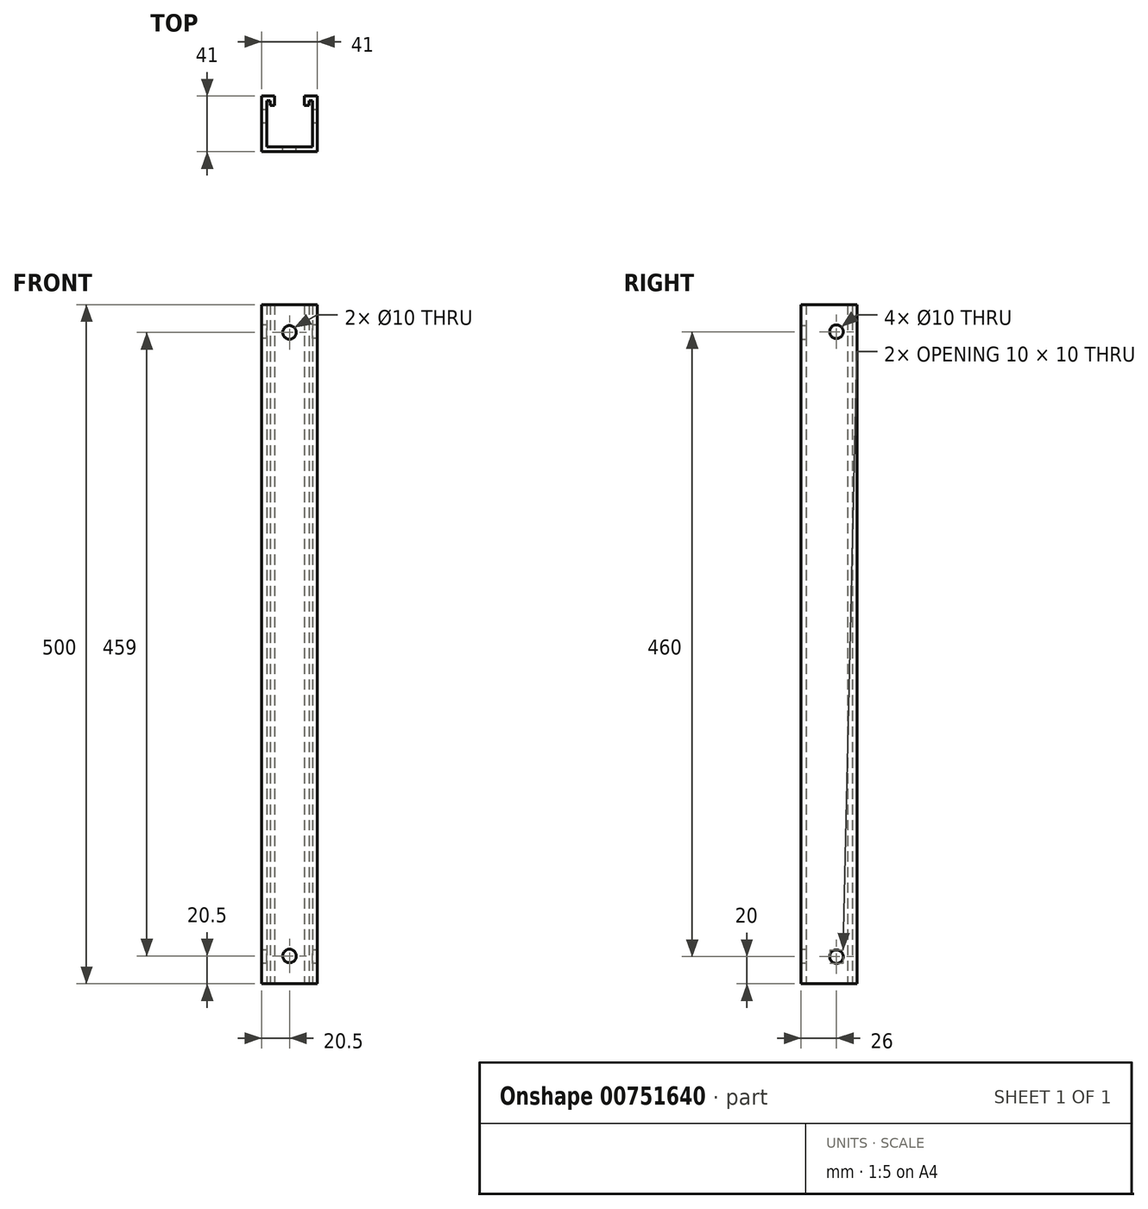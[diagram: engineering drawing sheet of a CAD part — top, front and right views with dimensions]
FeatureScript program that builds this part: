
annotation { "Feature Type Name" : "Feature", "Feature Type Description" : "" }
export const myFeature = defineFeature(function(context is Context, id is Id, definition is map)
    precondition{}
    {
        {
            var Q0;
            Q0=qCreatedBy(makeId("Top.planeOp"),FACE);
            var sketch = newSketch(context, id + "F0", { "sketchPlane" : qUnion([Q0])});
            skLineSegment(sketch, "E0", {"start": v(0, 0) * mm, "end": v(41, 0) * mm});
            skLineSegment(sketch, "E1", {"start": v(41, 0) * mm, "end": v(41, 41) * mm});
            skLineSegment(sketch, "E2", {"start": v(41, 41) * mm, "end": v(31.4, 41) * mm});
            skLineSegment(sketch, "E3", {"start": v(31.4, 41) * mm, "end": v(31.4, 34) * mm});
            skLineSegment(sketch, "E4", {"start": v(31.4, 34) * mm, "end": v(34.8, 34) * mm});
            skLineSegment(sketch, "E5", {"start": v(34.8, 34) * mm, "end": v(34.8, 37.5) * mm});
            skLineSegment(sketch, "E6", {"start": v(34.8, 37.5) * mm, "end": v(37.3, 37.5) * mm});
            skLineSegment(sketch, "E7", {"start": v(37.3, 37.5) * mm, "end": v(37.3, 3.7) * mm});
            skLineSegment(sketch, "E8", {"start": v(37.3, 3.7) * mm, "end": v(3.7, 3.7) * mm});
            skLineSegment(sketch, "E9", {"start": v(0, 0) * mm, "end": v(0, 41) * mm});
            skLineSegment(sketch, "E10", {"start": v(0, 41) * mm, "end": v(9.6, 41) * mm});
            skLineSegment(sketch, "E11", {"start": v(9.6, 41) * mm, "end": v(9.6, 34) * mm});
            skLineSegment(sketch, "E12", {"start": v(9.6, 34) * mm, "end": v(6.2, 34) * mm});
            skLineSegment(sketch, "E13", {"start": v(6.2, 34) * mm, "end": v(6.2, 37.5) * mm});
            skLineSegment(sketch, "E14", {"start": v(6.2, 37.5) * mm, "end": v(3.7, 37.5) * mm});
            skLineSegment(sketch, "E15", {"start": v(3.7, 37.5) * mm, "end": v(3.7, 3.7) * mm});
            skSolve(sketch);
        }
        {
            var Q0;
            Q0=qSketchRegion(id+"F0",true);
            extrude(context, id + "F1", {"entities" : qUnion([Q0]), "depth" : 500 * mm});
        }
        {
            var Q0;
            Q0=makeQuery(id+"F1.opExtrude","SWEPT_FACE",FACE,{"disambiguationData":[OSD([sQuery(id+"F0.wireOp",EDGE,"E8")])]});
            var sketch = newSketch(context, id + "F2", { "sketchPlane" : qUnion([Q0])});
            skCircle(sketch, "E16", {"center": v(-20.5, 479.5) * mm, "radius": 5 * mm});
            skPoint(sketch, "E16.centerSnap0", {"position": v(-20.5, 500) * mm});
            skCircle(sketch, "E17", {"center": v(-20.5, 20.5) * mm, "radius": 5 * mm});
            skPoint(sketch, "E17.centerSnap0", {"position": v(-20.5, 0) * mm});
            skSolve(sketch);
        }
        {
            var Q0;
            Q0=qSketchRegion(id+"F2",true);
            extrude(context, id + "F3", {"entities" : qUnion([Q0]), "operationType" : NewBodyOperationType.REMOVE, "endBound" : BoundingType.UP_TO_NEXT, "oppositeDirection" : true, "depth" : 25 * mm});
        }
        {
            var Q0;
            Q0=makeQuery(id+"F1.opExtrude","SWEPT_FACE",FACE,{"disambiguationData":[OSD([sQuery(id+"F0.wireOp",EDGE,"E9")])]});
            var sketch = newSketch(context, id + "F4", { "sketchPlane" : qUnion([Q0])});
            skCircle(sketch, "E18", {"center": v(-26, 20) * mm, "radius": 5 * mm});
            skCircle(sketch, "E19", {"center": v(-26, 480) * mm, "radius": 5 * mm});
            skSolve(sketch);
        }
        {
            var Q0;
            Q0=qSketchRegion(id+"F4",true);
            extrude(context, id + "F5", {"entities" : qUnion([Q0]), "operationType" : NewBodyOperationType.REMOVE, "endBound" : BoundingType.THROUGH_ALL, "oppositeDirection" : true, "depth" : 25 * mm});
        }
    });
